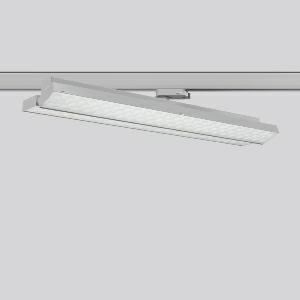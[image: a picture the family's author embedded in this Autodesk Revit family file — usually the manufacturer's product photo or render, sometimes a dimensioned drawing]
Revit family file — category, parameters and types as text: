
# Revit family: tx-move_742162_004_84eb
name_source: partatom
category: Lighting Fixtures
units: mm (PartAtom-declared; Revit-internal decimal feet)

## family parameters
Cut with Voids When Loaded = No
Host = Face
Light Source = No
Part Type = Normal
Room Calculation Point = No
Round Connector Dimension = Use Diameter
Shared = No

## types (1)
- MultiLumen 1 (1 x LED Modul 830, 2925 lm, 3000)
    Apparent Load = 41 VA
    CIE Flux Codes = 77 96 99 100 100
    Color Rendering = 80
    Color Temperature = 3000
    Default Elevation = 1800 mm
    Description = Series: TX-MOVE
Multifunctional surface-mounted spotlight for area lighting. Very flat design. Housing: sheet steel, powder-coated. Rotation range: 356°. Swivel range: 90°. Consistent alignment possible with visible tilt scale. High-efficiency LED units with optimum light control thanks to clear plastic (PC) lens optics. Spezielle Mikrostrukturen reduzieren Gelbsaum. Symmetrical light distribution. With multi adaptor for 3-circuit tracks 230 V. Suitable for Track on ceiling. MultiLumen: Luminous flux adjustable in 3 steps. Factory setting is the highest luminous flux. Environmentally friendly and resource-saving due to replaceable and recyclable components. 
Colour: silver, matt (approx. RAL 9006)
Length: 570 mm
Width: 119 mm
Height: 92 mm
Lamp: LED
Socket: without socket
Colour temperature: 3000K
Colour rendering index (CRI): 80
System power: 41 W
Rated luminous flux: 5850 lm
Luminous efficiency: 143 lm/W
System power 2: 57 W
Rated luminous flux 2: 7950 lm
Luminous efficiency 2: 139 lm/W
System power 3: 73 W
Rated luminous flux 3: 9700 lm
Luminous efficiency 3: 133 lm/W
Control gear: Regulated power supply
Protection class: I
Type of protection: IP 20
    Height = 75 mm
    Lamp = 1 x LED Modul 830
    Lamp Light Flux = 2925 lm
    Lamp count = 1
    Length = 569 mm
    Lifetime = 50000 h
    Luminous efficacy = 143 lm/W
    Manufacturer = RZB
    ModVariant = No
    Model = 742162.004
    Mounting Place = Ceiling
    Mounting Type = Surface mounted
    Number of Poles = 1
    OnlyDefault = Yes
    Power Factor = 1
    Product Name = TX-MOVE
    Product group = Track mounted projectors
    ProductGroupID = 301
    Protection Class = Protection class I
    Protection Degree = IP 20
    RLX_Detail_Level = 1
    RLX_Emergency_Light_Flux = 0 lm
    RLX_Emergency_Type = 0
    RLX_Emergency_Type_DB = No
    RlxData = <blob elided: 33101 chars, md5=b61aca75>
    Socket = socket
    Standby Power = 0 W
    System Light Flux = 5850 lm
    System Power = 41 W
    Type Comments = MultiLumen 1
    Type Image = 742162.004.jpg
    URL = http://relux.com
    VarID = multilumen_1
    Voltage = 0 V
    Weight = 0.00 kg
    Width = 119 mm

## geometry (parser evidence)
native form markers: Blend x4, Sweep x14
no freeform markers — native parametric forms only
